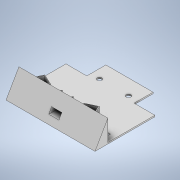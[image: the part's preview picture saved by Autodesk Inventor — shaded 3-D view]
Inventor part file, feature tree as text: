
AUTODESK INVENTOR PART (.ipt)
format: ipt  version: 2021 (Build 250183000, 183)  size: 319,488 bytes
history: native  units: mm
features: sketch x11, extrude x10, other x1
ambient origin geometry x8: Origin, YZ Plane, XZ Plane, XY Plane, X Axis, Y Axis, Z Axis, Center Point
bodies: Body1 (feature_tree)
feature tree (22):
  other  "Sólido1"
  extrude  "Base"  Depth=1.5mm TaperAngle=0.0deg
  extrude  "Angulo Base"  Depth=98.0mm TaperAngle=0.0deg
  extrude  "Extrusión3"  Depth=98.0mm TaperAngle=0.0deg
  extrude  "Extrusión4"  Depth=0.9mm
  extrude  "Extrusión5"  Depth=3.9mm
  extrude  "Extrusión6"  Depth=5.6mm
  extrude  "Extrusión7"  Depth=42.5mm
  extrude  "Extrusión8"  Depth=76.25mm TaperAngle=0.0deg
  extrude  "Extrusión9"  Depth=13.0mm
  extrude  "Extrusión11"  Depth=20.0mm TaperAngle=0.0deg
  sketch  "Boceto15"  dims[d57=4.84mm d58=6.076mm d59=11.2mm d60=0.9mm d61=4.978mm d62=11.2mm d63=0.9mm d64=0.0mm d65=5.25mm d66=0.0mm d67=3.8mm d68=11.2mm d69=10.054mm d70=0.0mm d76=4.84mm d77=1.0mm d78=3.9mm d79=0.0mm d93=0.93988mm d94=13.0mm d95=4.5mm d96=17.088mm d97=17.088mm d98=4.363323mm d99=0.7mm d100=0.9mm d101=90.0deg d102=0.9mm d103=0.9mm d104=0.7mm d105=10.0mm d106=0.0mm d71=0.5mm d72=0.872665mm d73=0.5mm d74=0.872665mm]
  sketch  "Boceto1"  dims[d0=3.5mm d1=0.0mm d2=87.0mm d3=21.0mm d4=12.0mm d5=23.0mm d6=98.0mm d7=7.5mm d8=7.5mm d9=79.5mm d10=2.1mm d11=9.0mm d12=11.0mm d13=16.0mm d14=1.0mm d15=3.6mm d16=2.1mm d17=1.3mm d18=5.0mm d19=36.0mm d20=9.5mm d21=5.0mm d22=17.0mm d23=10.0mm d24=8.7mm d25=4.3mm d26=4.0mm d27=11.0mm d28=54.0mm d29=2.85mm d30=1.5mm d31=0.0mm]
  sketch  "Boceto2"  dims[d32=20.935224mm d33=98.0mm d34=0.0mm]
  sketch  "Boceto3"  dims[d35=0.0mm d36=98.0mm d37=0.0mm]
  sketch  "Boceto4"  dims[d38=13.0mm d39=0.9mm]
  sketch  "Boceto5"  dims[d40=0.9mm d41=3.9mm]
  sketch  "Boceto6"  dims[d42=5.6mm d43=18.7mm]
  sketch  "Boceto7"  dims[d44=42.5mm d45=42.5mm]
  sketch  "Boceto8"  dims[d46=3.5mm d47=76.25mm d48=0.0mm]
  sketch  "Boceto9"  dims[d49=11.2mm d50=14.8mm d51=1.5mm d52=0.0mm d53=13.0mm]
  sketch  "Boceto14"  dims[d54=4.5mm d55=20.0mm d56=0.0mm]
